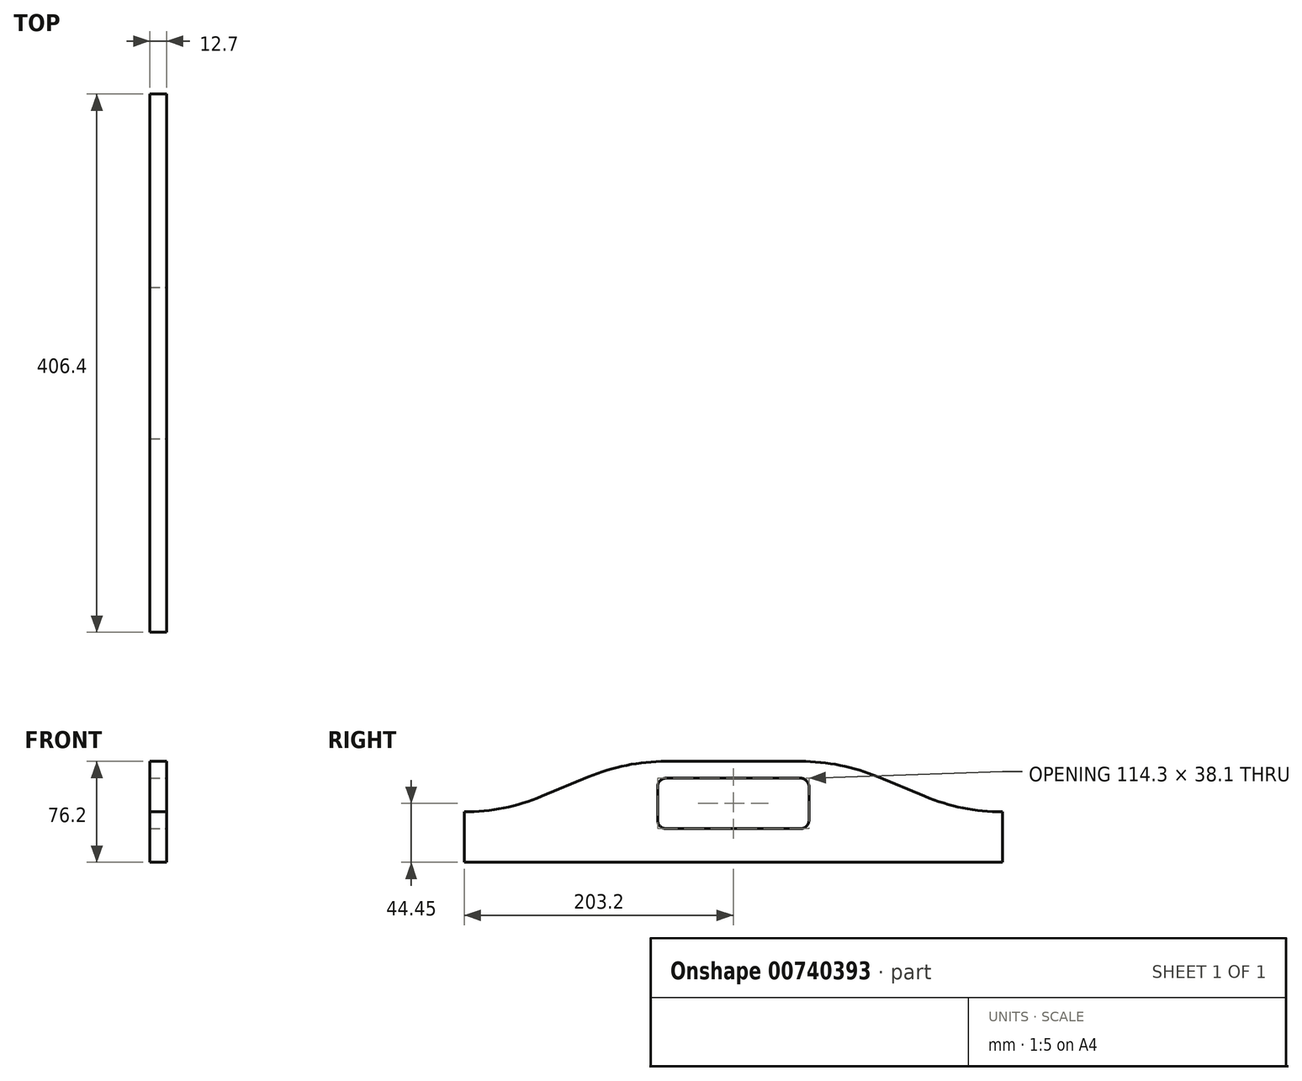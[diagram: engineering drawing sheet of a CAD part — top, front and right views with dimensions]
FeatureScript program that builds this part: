
annotation { "Feature Type Name" : "Feature", "Feature Type Description" : "" }
export const myFeature = defineFeature(function(context is Context, id is Id, definition is map)
    precondition{}
    {
        {
            var Q0;
            Q0=qCreatedBy(makeId("Right.planeOp"),FACE);
            var sketch = newSketch(context, id + "F0", { "sketchPlane" : qUnion([Q0])});
            skLineSegment(sketch, "E0.bottom", {"start": v(203.2, 38.1) * mm, "end": v(-203.2, 38.1) * mm});
            skLineSegment(sketch, "E0.top", {"start": v(203.2, -38.1) * mm, "end": v(-203.2, -38.1) * mm});
            skLineSegment(sketch, "E0.left", {"start": v(203.2, 38.1) * mm, "end": v(203.2, -38.1) * mm});
            skLineSegment(sketch, "E0.right", {"start": v(-203.2, 38.1) * mm, "end": v(-203.2, -38.1) * mm});
            skPoint(sketch, "E0.middle", {"position": v(0, 0) * mm});
            skSolve(sketch);
        }
        {
            var Q0;
            Q0=makeQuery(id+"F0.imprint","IMPRINT",FACE,{"disambiguationData":[TD([[makeQuery(id+"F0.imprint","IMPRINT",EDGE,{"derivedFrom":sQuery(id+"F0.wireOp",EDGE,"E0.bottom")}),1.0]])]});
            extrude(context, id + "F1", {"entities" : qUnion([Q0]), "depth" : 12.7 * mm, "offsetDistance" : 25.4 * mm});
        }
        {
            var Q0;
            Q0=makeQuery(id+"F1.opExtrude","CAP_FACE",FACE,{"disambiguationData":[OSD([sQuery(id+"F0.wireOp",EDGE,"E0.bottom"),sQuery(id+"F0.wireOp",EDGE,"E0.top"),sQuery(id+"F0.wireOp",EDGE,"E0.left"),sQuery(id+"F0.wireOp",EDGE,"E0.right")])],"isStart":false});
            var sketch = newSketch(context, id + "F2", { "sketchPlane" : qUnion([Q0])});
            skLineSegment(sketch, "E1.bottom", {"start": v(-50.8, 25.4) * mm, "end": v(50.8, 25.4) * mm});
            skLineSegment(sketch, "E1.top", {"start": v(-50.8, -12.7) * mm, "end": v(50.8, -12.7) * mm});
            skLineSegment(sketch, "E1.left", {"start": v(-57.15, 19.05) * mm, "end": v(-57.15, -6.35) * mm});
            skLineSegment(sketch, "E1.right", {"start": v(57.15, 19.05) * mm, "end": v(57.15, -6.35) * mm});
            skLineSegment(sketch, "E2", {"start": v(0, 25.4) * mm, "end": v(0, -12.7) * mm, "construction": true});
            skPoint(sketch, "E3.visualSharp", {"position": v(-57.15, 25.4) * mm});
            skArc(sketch, "E3.filletArc", {"start": v(-50.8, 25.4) * mm, "mid": v(-55.3, 23.54) * mm, "end": v(-57.15, 19.05) * mm});
            skPoint(sketch, "E4.visualSharp", {"position": v(57.15, 25.4) * mm});
            skArc(sketch, "E4.filletArc", {"start": v(57.15, 19.05) * mm, "mid": v(55.3, 23.54) * mm, "end": v(50.8, 25.4) * mm});
            skPoint(sketch, "E5.visualSharp", {"position": v(57.15, -12.7) * mm});
            skArc(sketch, "E5.filletArc", {"start": v(50.8, -12.7) * mm, "mid": v(55.3, -10.84) * mm, "end": v(57.15, -6.35) * mm});
            skPoint(sketch, "E6.visualSharp", {"position": v(-57.15, -12.7) * mm});
            skArc(sketch, "E6.filletArc", {"start": v(-57.15, -6.35) * mm, "mid": v(-55.3, -10.84) * mm, "end": v(-50.8, -12.7) * mm});
            skSolve(sketch);
        }
        {
            var Q0;
            Q0=makeQuery(id+"F2.imprint","IMPRINT",FACE,{"disambiguationData":[TD([[makeQuery(id+"F2.imprint","IMPRINT",EDGE,{"derivedFrom":sQuery(id+"F2.wireOp",EDGE,"E1.bottom")}),-1.0]])]});
            extrude(context, id + "F3", {"entities" : qUnion([Q0]), "operationType" : NewBodyOperationType.REMOVE, "oppositeDirection" : true, "depth" : 62.48 * mm, "offsetDistance" : 25.4 * mm});
        }
        {
            var Q0;
            Q0=makeQuery(id+"F1.opExtrude","CAP_FACE",FACE,{"disambiguationData":[OSD([sQuery(id+"F0.wireOp",EDGE,"E0.bottom"),sQuery(id+"F0.wireOp",EDGE,"E0.top"),sQuery(id+"F0.wireOp",EDGE,"E0.left"),sQuery(id+"F0.wireOp",EDGE,"E0.right")])],"isStart":false});
            var sketch = newSketch(context, id + "F4", { "sketchPlane" : qUnion([Q0])});
            skLineSegment(sketch, "E7", {"start": v(-203.2, 0) * mm, "end": v(-228.6, 0) * mm, "construction": true});
            skLineSegment(sketch, "E8", {"start": v(-203.2, 0) * mm, "end": v(-203.2, 38.1) * mm});
            skLineSegment(sketch, "E9", {"start": v(-203.2, 38.1) * mm, "end": v(-50.8, 38.1) * mm});
            skLineSegment(sketch, "E10", {"start": v(-144.58, 11.72) * mm, "end": v(-109.42, 26.38) * mm});
            skArc(sketch, "E11", {"start": v(-203.2, 0) * mm, "mid": v(-173.31, 2.96) * mm, "end": v(-144.58, 11.72) * mm});
            skArc(sketch, "E12", {"start": v(-50.8, 38.1) * mm, "mid": v(-80.69, 35.14) * mm, "end": v(-109.42, 26.38) * mm});
            skLineSegment(sketch, "E13.MirrorCS", {"start": v(144.58, 11.72) * mm, "end": v(109.42, 26.38) * mm});
            skArc(sketch, "E14.MirrorCS", {"start": v(50.8, 38.1) * mm, "mid": v(80.69, 35.14) * mm, "end": v(109.42, 26.38) * mm});
            skLineSegment(sketch, "E15.MirrorCS", {"start": v(203.2, 38.1) * mm, "end": v(50.8, 38.1) * mm});
            skLineSegment(sketch, "E16.MirrorCS", {"start": v(203.2, 0) * mm, "end": v(203.2, 38.1) * mm});
            skArc(sketch, "E17.MirrorCS", {"start": v(203.2, 0) * mm, "mid": v(173.31, 2.96) * mm, "end": v(144.58, 11.72) * mm});
            skSolve(sketch);
        }
        {
            var Q0;
            {var subQ0=sQuery(id+"F4.wireOp",EDGE,"E8");Q0=makeQuery(id+"F4.imprint","IMPRINT",FACE,{"disambiguationData":[TD([[makeQuery(id+"F4.imprint","IMPRINT",EDGE,{"derivedFrom":subQ0}),1.0]])]});}
            var Q1;
            Q1=makeQuery(id+"F4.imprint","IMPRINT",FACE,{"disambiguationData":[TD([[makeQuery(id+"F4.imprint","IMPRINT",EDGE,{"derivedFrom":sQuery(id+"F4.wireOp",EDGE,"E13.MirrorCS")}),-1.0]])]});
            extrude(context, id + "F5", {"entities" : qUnion([Q0, Q1]), "operationType" : NewBodyOperationType.REMOVE, "oppositeDirection" : true, "depth" : 38.6 * mm, "offsetDistance" : 25.4 * mm});
        }
    });
